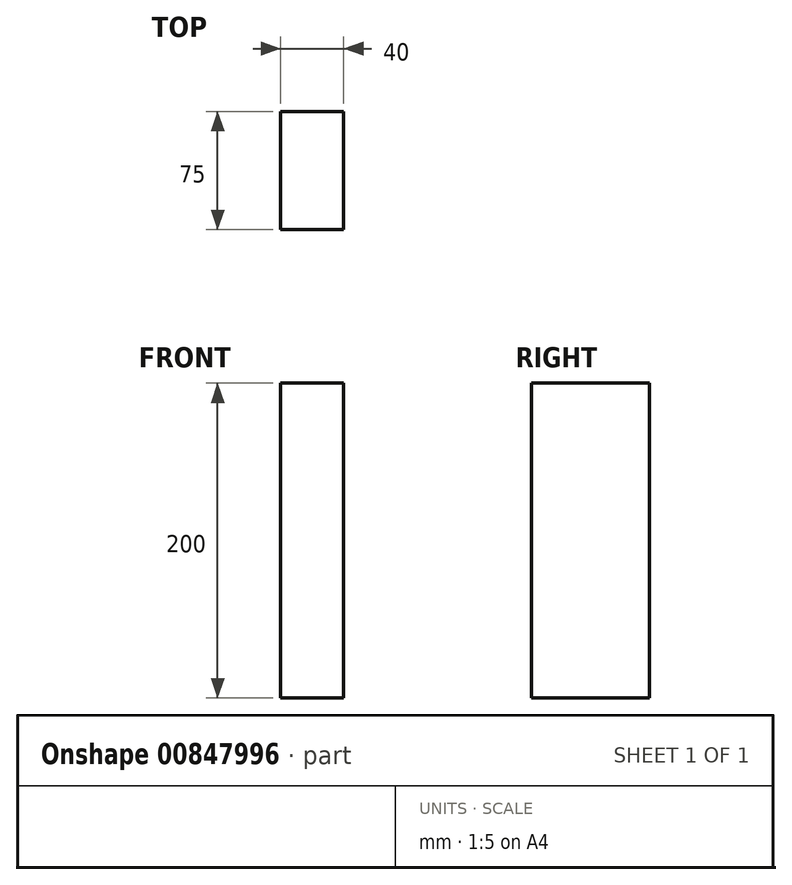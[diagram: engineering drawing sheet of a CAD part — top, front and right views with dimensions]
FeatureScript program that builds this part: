
annotation { "Feature Type Name" : "Feature", "Feature Type Description" : "" }
export const myFeature = defineFeature(function(context is Context, id is Id, definition is map)
    precondition{}
    {
        {
            var Q0;
            Q0=qCreatedBy(makeId("Top.planeOp"),FACE);
            var sketch = newSketch(context, id + "F0", { "sketchPlane" : qUnion([Q0])});
            skPoint(sketch, "E0", {"position": v(24.42, 0) * mm});
            skPoint(sketch, "E1", {"position": v(0, 0) * mm});
            skLineSegment(sketch, "E2", {"start": v(0, 0) * mm, "end": v(0, 35.6) * mm});
            skLineSegment(sketch, "E3", {"start": v(0, 0) * mm, "end": v(0, -39.4) * mm});
            skLineSegment(sketch, "E4", {"start": v(0, 35.6) * mm, "end": v(40, 35.6) * mm});
            skLineSegment(sketch, "E5", {"start": v(40, 35.6) * mm, "end": v(40, -39.4) * mm});
            skLineSegment(sketch, "E6", {"start": v(0, -39.4) * mm, "end": v(40, -39.4) * mm});
            skSolve(sketch);
        }
        {
            var Q0;
            Q0=makeQuery(id+"F0.imprint","IMPRINT",FACE,{"disambiguationData":[TD([[makeQuery(id+"F0.imprint","IMPRINT",EDGE,{"derivedFrom":sQuery(id+"F0.wireOp",EDGE,"E2")}),-1.0]])]});
            extrude(context, id + "F1", {"entities" : qUnion([Q0]), "depth" : 200 * mm, "offsetDistance" : 25 * mm});
        }
    });
